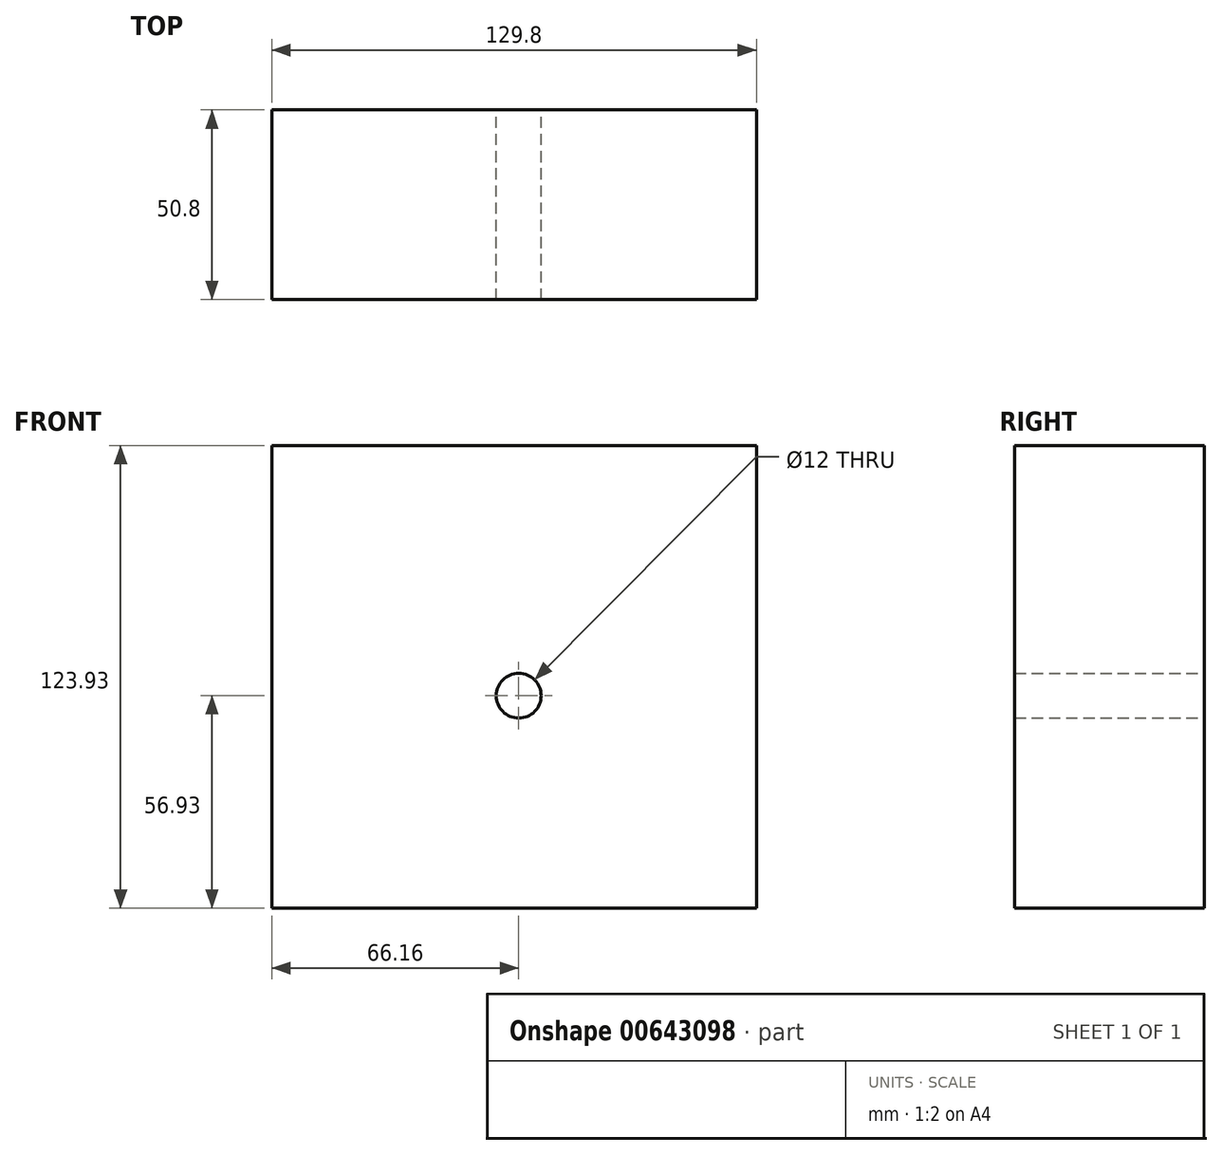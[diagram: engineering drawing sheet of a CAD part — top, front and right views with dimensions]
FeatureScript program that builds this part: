
annotation { "Feature Type Name" : "Feature", "Feature Type Description" : "" }
export const myFeature = defineFeature(function(context is Context, id is Id, definition is map)
    precondition{}
    {
        {
            var Q0;
            Q0=qCreatedBy(makeId("Front.planeOp"),FACE);
            var sketch = newSketch(context, id + "F0", { "sketchPlane" : qUnion([Q0])});
            skLineSegment(sketch, "E0.bottom", {"start": v(-66.16, 67) * mm, "end": v(63.64, 67) * mm});
            skLineSegment(sketch, "E0.top", {"start": v(-66.16, -56.93) * mm, "end": v(63.64, -56.93) * mm});
            skLineSegment(sketch, "E0.left", {"start": v(-66.16, 67) * mm, "end": v(-66.16, -56.93) * mm});
            skLineSegment(sketch, "E0.right", {"start": v(63.64, 67) * mm, "end": v(63.64, -56.93) * mm});
            skSolve(sketch);
        }
        {
            var Q0;
            Q0=makeQuery(id+"F0.imprint","IMPRINT",FACE,{"disambiguationData":[TD([[makeQuery(id+"F0.imprint","IMPRINT",EDGE,{"derivedFrom":sQuery(id+"F0.wireOp",EDGE,"E0.bottom")}),-1.0]])]});
            extrude(context, id + "F1", {"entities" : qUnion([Q0]), "depth" : 25.4 * mm, "offsetDistance" : 25.4 * mm});
        }
        {
            var Q0;
            Q0=makeQuery(id+"F1.opExtrude","CAP_FACE",FACE,{"disambiguationData":[OSD([sQuery(id+"F0.wireOp",EDGE,"E0.bottom"),sQuery(id+"F0.wireOp",EDGE,"E0.top"),sQuery(id+"F0.wireOp",EDGE,"E0.left"),sQuery(id+"F0.wireOp",EDGE,"E0.right")])],"isStart":false});
            extrude(context, id + "F2", {"entities" : qUnion([Q0]), "operationType" : NewBodyOperationType.ADD, "depth" : 25.4 * mm, "offsetDistance" : 25.4 * mm});
        }
        {
            var Q0;
            Q0=makeQuery(id+"F1.opExtrude","CAP_FACE",FACE,{"disambiguationData":[OSD([sQuery(id+"F0.wireOp",EDGE,"E0.bottom"),sQuery(id+"F0.wireOp",EDGE,"E0.top"),sQuery(id+"F0.wireOp",EDGE,"E0.left"),sQuery(id+"F0.wireOp",EDGE,"E0.right")])],"isStart":true});
            var sketch = newSketch(context, id + "F3", { "sketchPlane" : qUnion([Q0])});
            skCircle(sketch, "E1", {"center": v(0, 0) * mm, "radius": 6 * mm});
            skSolve(sketch);
        }
        {
            var Q0;
            Q0=makeQuery(id+"F3.imprint","IMPRINT",FACE,{"disambiguationData":[TD([[makeQuery(id+"F3.imprint","IMPRINT",EDGE,{"derivedFrom":sQuery(id+"F3.wireOp",EDGE,"E1")}),1.0]])]});
            extrude(context, id + "F4", {"entities" : qUnion([Q0]), "operationType" : NewBodyOperationType.REMOVE, "oppositeDirection" : true, "depth" : 78.49 * mm, "offsetDistance" : 25.4 * mm});
        }
    });
